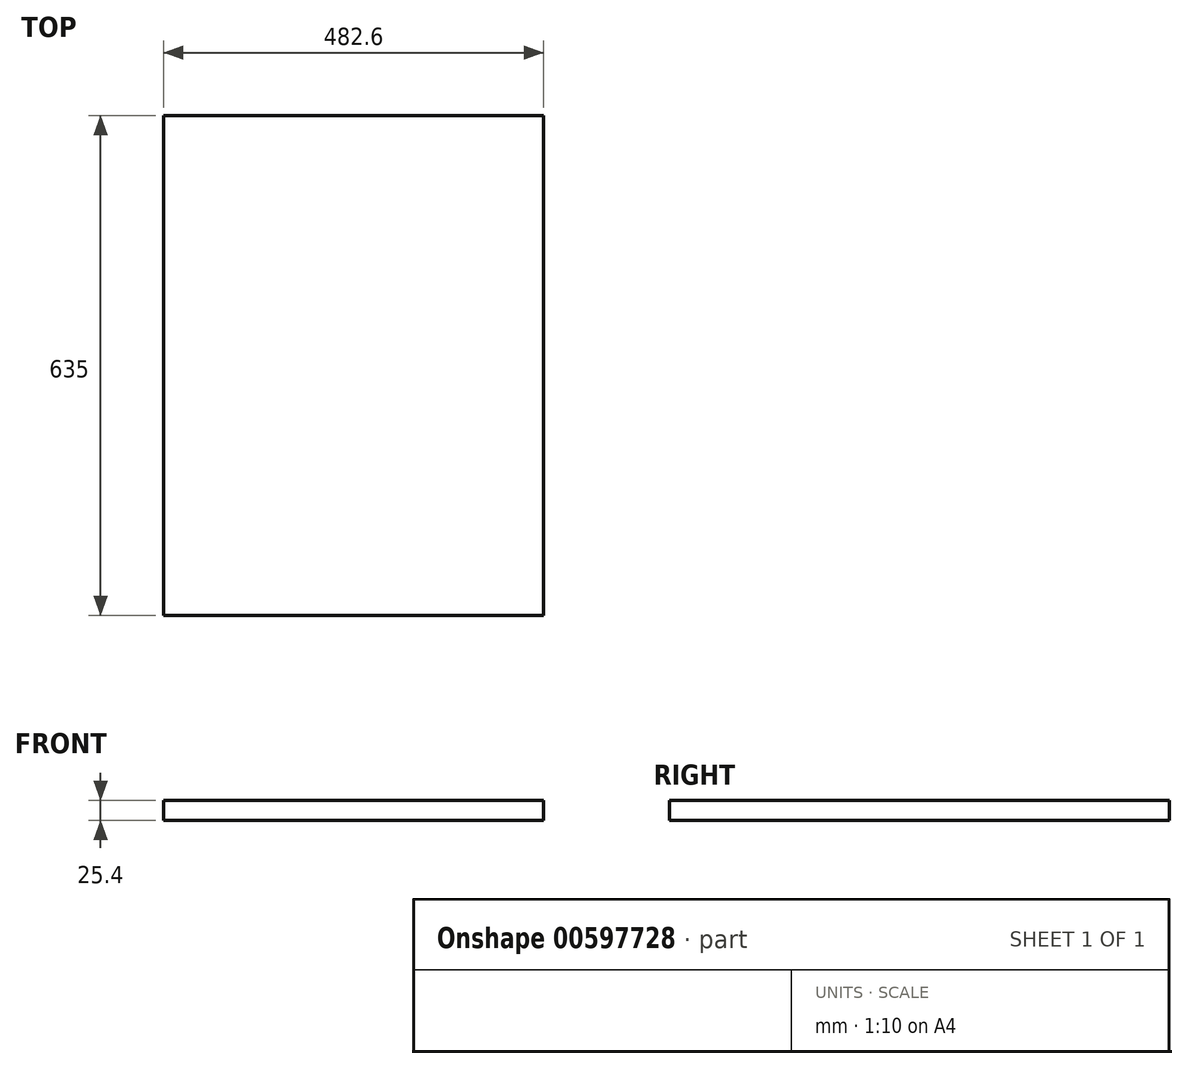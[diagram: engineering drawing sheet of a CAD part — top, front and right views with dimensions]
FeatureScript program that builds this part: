
annotation { "Feature Type Name" : "Feature", "Feature Type Description" : "" }
export const myFeature = defineFeature(function(context is Context, id is Id, definition is map)
    precondition{}
    {
        {
            var Q0;
            Q0=qCreatedBy(makeId("Top.planeOp"),FACE);
            var sketch = newSketch(context, id + "F0", { "sketchPlane" : qUnion([Q0])});
            skLineSegment(sketch, "E0.bottom", {"start": v(0, 635) * mm, "end": v(482.6, 635) * mm});
            skLineSegment(sketch, "E0.top", {"start": v(0, 0) * mm, "end": v(482.6, 0) * mm});
            skLineSegment(sketch, "E0.left", {"start": v(0, 635) * mm, "end": v(0, 0) * mm});
            skLineSegment(sketch, "E0.right", {"start": v(482.6, 635) * mm, "end": v(482.6, 0) * mm});
            skSolve(sketch);
        }
        {
            var Q0;
            Q0 = qSketchRegion(id + "F0", true);
            extrude(context, id + "F1", {"entities" : qUnion([Q0]), "depth" : 25.4 * mm, "offsetDistance" : 25.4 * mm});
        }
    });
